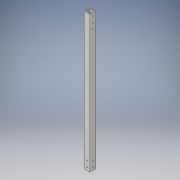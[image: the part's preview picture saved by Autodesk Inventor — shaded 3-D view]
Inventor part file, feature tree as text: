
AUTODESK INVENTOR PART (.ipt)
format: ipt  version: 2018 (Build 220112000, 112)  size: 141,824 bytes
history: native  units: in
note: dims shown in document units (in); Inventor stores cm internally (conversion verified against a paired STEP export)
features: extrude x4, sketch x4
ambient origin geometry x8: Origin, YZ Plane, XZ Plane, XY Plane, X Axis, Y Axis, Z Axis, Center Point
bodies: Solid1 (feature_tree)
feature tree (8):
  extrude  "Extrusion1"  Depth=1.0in
  extrude  "Extrusion2"  Depth=24.0in TaperAngle=0.0deg
  extrude  "Extrusion3"  Depth=1.0in
  extrude  "Extrusion4"  Depth=1.0in
  sketch  "Sketch1"  dims[d0=1.0in d1=1.0in]
  sketch  "Sketch2"  dims[d2=0.125in d3=24.0in d4=0.0in]
  sketch  "Sketch3"  dims[d5=0.5in d6=1.0in]
  sketch  "Sketch4"  dims[d7=0.5in d8=1.0in d9=0.2031in d10=0.2031in d11=0.2031in d12=0.2031in d13=25.0in d14=0.0in d15=1.0in d16=0.2031in d17=5.0in d18=0.0in d19=0.5in d20=1.0in d21=0.2031in d22=0.2031in d23=5.0in d24=0.0in]
